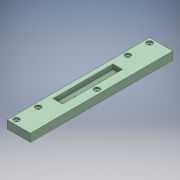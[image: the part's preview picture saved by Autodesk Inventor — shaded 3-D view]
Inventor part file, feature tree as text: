
AUTODESK INVENTOR PART (.ipt)
format: ipt  version: 2016 (Build 200138000, 138)  size: 157,696 bytes
history: native  units: mm
features: sketch x4, extrude x2, hole x2, mirror x1
ambient origin geometry x8: Origin, YZ Plane, XZ Plane, XY Plane, X Axis, Y Axis, Z Axis, Center Point
bodies: Solid1 (feature_tree)
feature tree (9):
  extrude  "baseExtrusion"  Depth=45.0mm
  hole  "xyStageAttatchM5"  [1 undecoded]
  extrude  "Extrusion2"  Depth=10.0mm
  hole  "Hole2"  [1 undecoded]
  mirror  "Mirror1"
  sketch  "Sketch1"  dims[d0=30.0mm d1=45.0mm]
  sketch  "Sketch2"  dims[d2=460.0mm d3=230.0mm]
  sketch  "Sketch3"  dims[d4=10.0mm d5=0.0mm d6=80.0mm]
  sketch  "Sketch4"  dims[d7=40.0mm d8=30.0mm d9=30.0mm d10=4.134mm d11=10.0mm d12=4.0mm d13=2.0mm d14=90.0deg d15=14.2mm d16=20.594885mm d17=194.066919mm d18=97.033459mm d19=30.783029mm d20=15.391515mm d21=16.0mm d22=0.0mm d23=15.0mm d24=70.0mm d25=6.6mm d26=6.0mm d27=18.0mm d28=4.8mm d29=90.0deg d30=8.0mm d31=20.594885mm d33=15.0mm d34=15.0mm]
note: 2 required parameter values undecoded (feature->parameter linkage not recoverable at this tier; creation-order binding heuristic only, values carry confidence <= 0.55)
